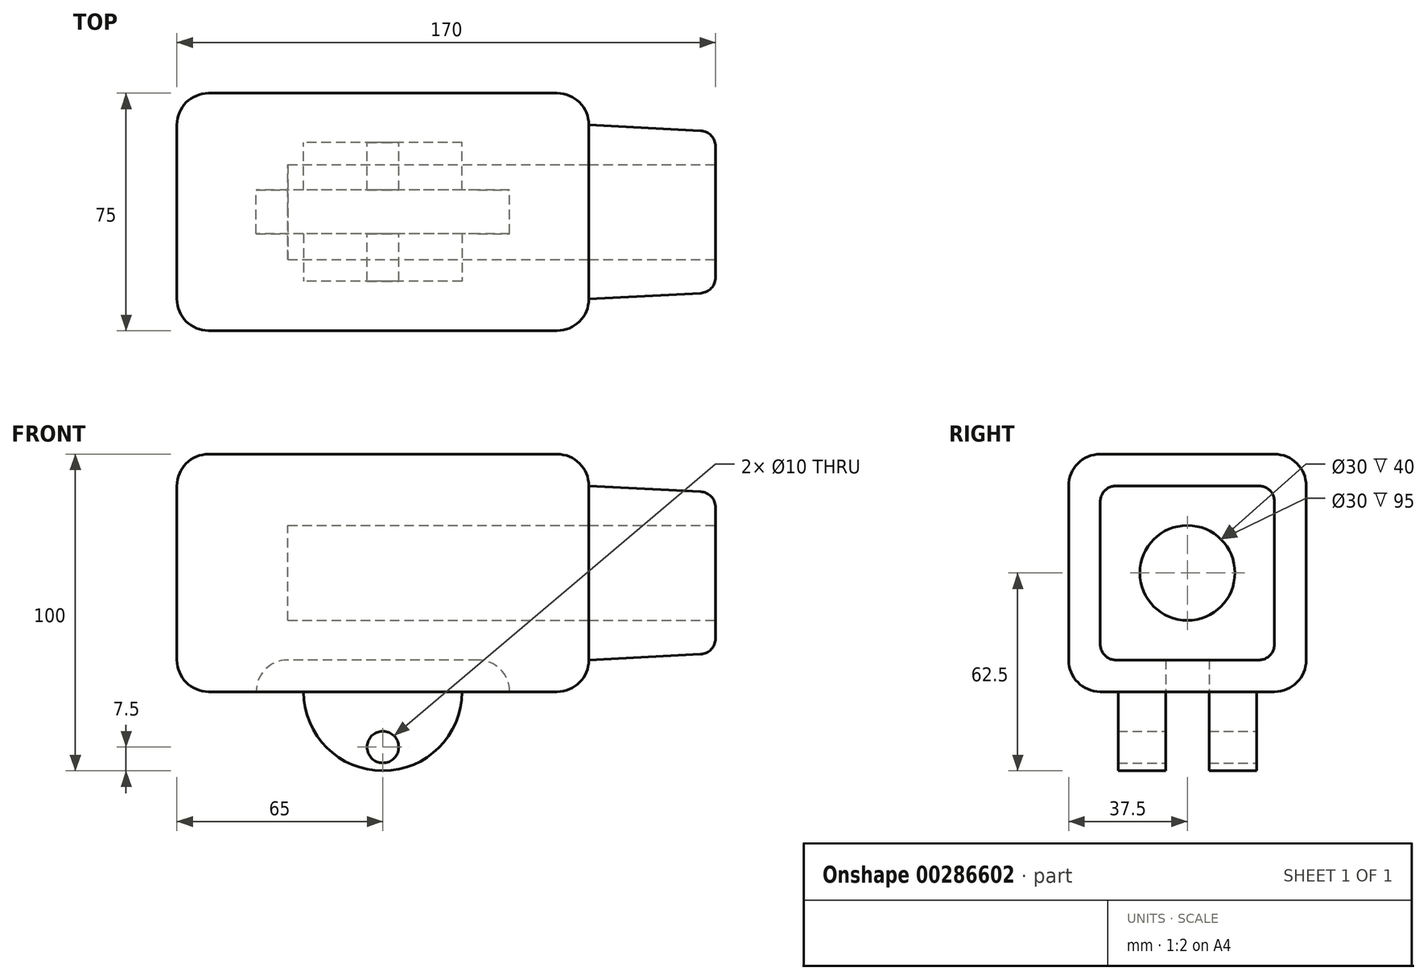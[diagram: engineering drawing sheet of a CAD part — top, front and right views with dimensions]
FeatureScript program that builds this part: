
annotation { "Feature Type Name" : "Feature", "Feature Type Description" : "" }
export const myFeature = defineFeature(function(context is Context, id is Id, definition is map)
    precondition{}
    {
        {
            var Q0;
            Q0=qCreatedBy(makeId("Top.planeOp"),FACE);
            var sketch = newSketch(context, id + "F0", { "sketchPlane" : qUnion([Q0])});
            skLineSegment(sketch, "E0.bottom", {"start": v(-65, 37.5) * mm, "end": v(65, 37.5) * mm});
            skLineSegment(sketch, "E0.top", {"start": v(-65, -37.5) * mm, "end": v(65, -37.5) * mm});
            skLineSegment(sketch, "E0.left", {"start": v(-65, 37.5) * mm, "end": v(-65, -37.5) * mm});
            skLineSegment(sketch, "E0.right", {"start": v(65, 37.5) * mm, "end": v(65, -37.5) * mm});
            skPoint(sketch, "E0.middle", {"position": v(0, 0) * mm});
            skSolve(sketch);
        }
        {
            var Q0;
            Q0=makeQuery(id+"F0.imprint","IMPRINT",FACE,{"disambiguationData":[TD([[makeQuery(id+"F0.imprint","IMPRINT",EDGE,{"derivedFrom":sQuery(id+"F0.wireOp",EDGE,"E0.bottom")}),-1.0]])]});
            extrude(context, id + "F1", {"entities" : qUnion([Q0]), "depth" : 75 * mm});
        }
        {
            var Q0;
            Q0=makeQuery(id+"F1.opExtrude","CAP_FACE",FACE,{"disambiguationData":[OSD([sQuery(id+"F0.wireOp",EDGE,"E0.bottom"),sQuery(id+"F0.wireOp",EDGE,"E0.top"),sQuery(id+"F0.wireOp",EDGE,"E0.left"),sQuery(id+"F0.wireOp",EDGE,"E0.right")])],"isStart":false});
            var Q1;
            Q1=makeQuery(id+"F1.opExtrude","SWEPT_FACE",FACE,{"disambiguationData":[OSD([sQuery(id+"F0.wireOp",EDGE,"E0.top")])]});
            var Q2;
            Q2=makeQuery(id+"F1.opExtrude","SWEPT_FACE",FACE,{"disambiguationData":[OSD([sQuery(id+"F0.wireOp",EDGE,"E0.right")])]});
            var Q3;
            Q3=makeQuery(id+"F1.opExtrude","SWEPT_FACE",FACE,{"disambiguationData":[OSD([sQuery(id+"F0.wireOp",EDGE,"E0.bottom")])]});
            var Q4;
            Q4=makeQuery(id+"F1.opExtrude","CAP_FACE",FACE,{"disambiguationData":[OSD([sQuery(id+"F0.wireOp",EDGE,"E0.bottom"),sQuery(id+"F0.wireOp",EDGE,"E0.top"),sQuery(id+"F0.wireOp",EDGE,"E0.left"),sQuery(id+"F0.wireOp",EDGE,"E0.right")])],"isStart":true});
            fillet(context, id + "F2", {"entities" : qUnion([Q0, Q1, Q2, Q3, Q4]), "radius" : 10 * mm, "tangentPropagation" : true, "allowEdgeOverflow" : false});
        }
        {
            var Q0;
            Q0=makeQuery(id+"F1.opExtrude","SWEPT_FACE",FACE,{"disambiguationData":[OSD([sQuery(id+"F0.wireOp",EDGE,"E0.right")])]});
            extrude(context, id + "F3", {"entities" : qUnion([Q0]), "depth" : 40 * mm, "hasDraft" : true, "draftAngle" : 3 * degree, "draftPullDirection" : true});
        }
        {
            var Q0;
            {var subQ0=sQuery(id+"F0.wireOp",EDGE,"E0.right");var subQ1=sQuery(id+"F0.wireOp",EDGE,"E0.top");Q0=makeQuery(id+"F3.opExtrude","SWEPT_EDGE",EDGE,{"disambiguationData":[OSD([subQ1,subQ0]),TDD([makeQuery(id+"F2.opFillet","BLEND_VERTEX",VERTEX,{"blendedFrom":[makeQuery(id+"F1.opExtrude","CAP_VERTEX",VERTEX,{"disambiguationData":[OSD([subQ1,subQ0])],"isStart":false}),makeQuery(id+"F1.opExtrude","SWEPT_EDGE",EDGE,{"disambiguationData":[OSD([subQ1,subQ0])]}),makeQuery(id+"F1.opExtrude","CAP_EDGE",EDGE,{"disambiguationData":[OSD([subQ0])],"isStart":false}),makeQuery(id+"F1.opExtrude","SWEPT_FACE",FACE,{"disambiguationData":[OSD([subQ0])]})],"blendedInto":[makeQuery(id+"F1.opExtrude","SWEPT_FACE",FACE,{"disambiguationData":[OSD([subQ0])]})]})])]});}
            var Q1;
            {var subQ0=sQuery(id+"F0.wireOp",EDGE,"E0.right");var subQ1=sQuery(id+"F0.wireOp",EDGE,"E0.bottom");Q1=makeQuery(id+"F3.opExtrude","SWEPT_EDGE",EDGE,{"disambiguationData":[OSD([subQ1,subQ0]),TDD([makeQuery(id+"F2.opFillet","BLEND_VERTEX",VERTEX,{"blendedFrom":[makeQuery(id+"F1.opExtrude","CAP_VERTEX",VERTEX,{"disambiguationData":[OSD([subQ1,subQ0])],"isStart":false}),makeQuery(id+"F1.opExtrude","SWEPT_EDGE",EDGE,{"disambiguationData":[OSD([subQ1,subQ0])]}),makeQuery(id+"F1.opExtrude","CAP_EDGE",EDGE,{"disambiguationData":[OSD([subQ0])],"isStart":false}),makeQuery(id+"F1.opExtrude","SWEPT_FACE",FACE,{"disambiguationData":[OSD([subQ0])]})],"blendedInto":[makeQuery(id+"F1.opExtrude","SWEPT_FACE",FACE,{"disambiguationData":[OSD([subQ0])]})]})])]});}
            var Q2;
            {var subQ0=sQuery(id+"F0.wireOp",EDGE,"E0.right");var subQ1=sQuery(id+"F0.wireOp",EDGE,"E0.bottom");Q2=makeQuery(id+"F3.opExtrude","SWEPT_EDGE",EDGE,{"disambiguationData":[OSD([subQ1,subQ0]),TDD([makeQuery(id+"F2.opFillet","BLEND_VERTEX",VERTEX,{"blendedFrom":[makeQuery(id+"F1.opExtrude","CAP_VERTEX",VERTEX,{"disambiguationData":[OSD([subQ1,subQ0])],"isStart":true}),makeQuery(id+"F1.opExtrude","SWEPT_EDGE",EDGE,{"disambiguationData":[OSD([subQ1,subQ0])]}),makeQuery(id+"F1.opExtrude","CAP_EDGE",EDGE,{"disambiguationData":[OSD([subQ0])],"isStart":true}),makeQuery(id+"F1.opExtrude","SWEPT_FACE",FACE,{"disambiguationData":[OSD([subQ0])]})],"blendedInto":[makeQuery(id+"F1.opExtrude","SWEPT_FACE",FACE,{"disambiguationData":[OSD([subQ0])]})]})])]});}
            var Q3;
            {var subQ0=sQuery(id+"F0.wireOp",EDGE,"E0.right");var subQ1=sQuery(id+"F0.wireOp",EDGE,"E0.top");Q3=makeQuery(id+"F3.opExtrude","SWEPT_EDGE",EDGE,{"disambiguationData":[OSD([subQ1,subQ0]),TDD([makeQuery(id+"F2.opFillet","BLEND_VERTEX",VERTEX,{"blendedFrom":[makeQuery(id+"F1.opExtrude","CAP_VERTEX",VERTEX,{"disambiguationData":[OSD([subQ1,subQ0])],"isStart":true}),makeQuery(id+"F1.opExtrude","SWEPT_EDGE",EDGE,{"disambiguationData":[OSD([subQ1,subQ0])]}),makeQuery(id+"F1.opExtrude","CAP_EDGE",EDGE,{"disambiguationData":[OSD([subQ0])],"isStart":true}),makeQuery(id+"F1.opExtrude","SWEPT_FACE",FACE,{"disambiguationData":[OSD([subQ0])]})],"blendedInto":[makeQuery(id+"F1.opExtrude","SWEPT_FACE",FACE,{"disambiguationData":[OSD([subQ0])]})]})])]});}
            var Q4;
            Q4=makeQuery(id+"F3.opExtrude","CAP_FACE",FACE,{"disambiguationData":[OSD([sQuery(id+"F0.wireOp",EDGE,"E0.right")])],"isStart":false});
            fillet(context, id + "F4", {"entities" : qUnion([Q0, Q1, Q2, Q3, Q4]), "radius" : 5 * mm, "tangentPropagation" : true, "allowEdgeOverflow" : false});
        }
        {
            var Q0;
            Q0=makeQuery(id+"F3.opExtrude","CAP_FACE",FACE,{"disambiguationData":[OSD([sQuery(id+"F0.wireOp",EDGE,"E0.right")])],"isStart":false});
            var sketch = newSketch(context, id + "F5", { "sketchPlane" : qUnion([Q0])});
            skCircle(sketch, "E1", {"center": v(0, 37.5) * mm, "radius": 15 * mm});
            skPoint(sketch, "E1.centerSnap0", {"position": v(-20.66, 37.5) * mm});
            skSolve(sketch);
        }
        {
            var Q0;
            Q0=makeQuery(id+"F5.imprint","IMPRINT",FACE,{"disambiguationData":[TD([[makeQuery(id+"F5.imprint","IMPRINT",EDGE,{"derivedFrom":sQuery(id+"F5.wireOp",EDGE,"E1")}),1.0]])]});
            extrude(context, id + "F6", {"entities" : qUnion([Q0]), "operationType" : NewBodyOperationType.REMOVE, "oppositeDirection" : true, "depth" : 135 * mm});
        }
        {
            var Q0;
            Q0=makeQuery(id+"F1.opExtrude","CAP_FACE",FACE,{"disambiguationData":[OSD([sQuery(id+"F0.wireOp",EDGE,"E0.bottom"),sQuery(id+"F0.wireOp",EDGE,"E0.top"),sQuery(id+"F0.wireOp",EDGE,"E0.left"),sQuery(id+"F0.wireOp",EDGE,"E0.right")])],"isStart":true});
            var sketch = newSketch(context, id + "F7", { "sketchPlane" : qUnion([Q0])});
            skLineSegment(sketch, "E2.bottom", {"start": v(25, 6.88) * mm, "end": v(-25, 6.88) * mm});
            skLineSegment(sketch, "E2.top", {"start": v(25, 21.88) * mm, "end": v(-25, 21.88) * mm});
            skLineSegment(sketch, "E2.left", {"start": v(25, 6.88) * mm, "end": v(25, 21.88) * mm});
            skLineSegment(sketch, "E2.right", {"start": v(-25, 6.88) * mm, "end": v(-25, 21.88) * mm});
            skPoint(sketch, "E2.middle", {"position": v(0, 14.38) * mm});
            skLineSegment(sketch, "E3.bottom", {"start": v(25, -6.88) * mm, "end": v(-25, -6.88) * mm});
            skLineSegment(sketch, "E3.top", {"start": v(25, -21.88) * mm, "end": v(-25, -21.88) * mm});
            skLineSegment(sketch, "E3.left", {"start": v(25, -6.88) * mm, "end": v(25, -21.88) * mm});
            skLineSegment(sketch, "E3.right", {"start": v(-25, -6.88) * mm, "end": v(-25, -21.88) * mm});
            skPoint(sketch, "E3.middle", {"position": v(0, -14.38) * mm});
            skSolve(sketch);
        }
        {
            var Q0;
            Q0=makeQuery(id+"F7.imprint","IMPRINT",FACE,{"disambiguationData":[TD([[makeQuery(id+"F7.imprint","IMPRINT",EDGE,{"derivedFrom":sQuery(id+"F7.wireOp",EDGE,"E3.bottom")}),1.0]])]});
            var Q1;
            Q1=makeQuery(id+"F7.imprint","IMPRINT",FACE,{"disambiguationData":[TD([[makeQuery(id+"F7.imprint","IMPRINT",EDGE,{"derivedFrom":sQuery(id+"F7.wireOp",EDGE,"E2.bottom")}),-1.0]])]});
            extrude(context, id + "F8", {"entities" : qUnion([Q0, Q1]), "operationType" : NewBodyOperationType.ADD, "depth" : 25 * mm});
        }
        {
            var Q0;
            Q0=makeQuery(id+"F8.opExtrude","CAP_EDGE",EDGE,{"disambiguationData":[OSD([sQuery(id+"F7.wireOp",EDGE,"E3.right")])],"isStart":false});
            var Q1;
            Q1=makeQuery(id+"F8.opExtrude","CAP_EDGE",EDGE,{"disambiguationData":[OSD([sQuery(id+"F7.wireOp",EDGE,"E3.left")])],"isStart":false});
            var Q2;
            Q2=makeQuery(id+"F8.opExtrude","CAP_EDGE",EDGE,{"disambiguationData":[OSD([sQuery(id+"F7.wireOp",EDGE,"E2.left")])],"isStart":false});
            var Q3;
            Q3=makeQuery(id+"F8.opExtrude","CAP_EDGE",EDGE,{"disambiguationData":[OSD([sQuery(id+"F7.wireOp",EDGE,"E2.right")])],"isStart":false});
            fillet(context, id + "F9", {"entities" : qUnion([Q0, Q1, Q2, Q3]), "radius" : 25 * mm, "tangentPropagation" : true, "allowEdgeOverflow" : false});
        }
        {
            var Q0;
            Q0=makeQuery(id+"F8.opExtrude","SWEPT_FACE",FACE,{"disambiguationData":[OSD([sQuery(id+"F7.wireOp",EDGE,"E3.top")])]});
            var sketch = newSketch(context, id + "F10", { "sketchPlane" : qUnion([Q0])});
            skCircle(sketch, "E4", {"center": v(0, -17.5) * mm, "radius": 5 * mm});
            skPoint(sketch, "E4.centerSnap0", {"position": v(0, -25) * mm});
            skSolve(sketch);
        }
        {
            var Q0;
            Q0=makeQuery(id+"F10.imprint","IMPRINT",FACE,{"disambiguationData":[TD([[makeQuery(id+"F10.imprint","IMPRINT",EDGE,{"derivedFrom":sQuery(id+"F10.wireOp",EDGE,"E4")}),1.0]])]});
            extrude(context, id + "F11", {"entities" : qUnion([Q0]), "operationType" : NewBodyOperationType.REMOVE, "endBound" : BoundingType.THROUGH_ALL, "oppositeDirection" : true, "depth" : 25 * mm});
        }
        {
            var Q0;
            Q0=makeQuery(id+"F1.opExtrude","CAP_FACE",FACE,{"disambiguationData":[OSD([sQuery(id+"F0.wireOp",EDGE,"E0.bottom"),sQuery(id+"F0.wireOp",EDGE,"E0.top"),sQuery(id+"F0.wireOp",EDGE,"E0.left"),sQuery(id+"F0.wireOp",EDGE,"E0.right")])],"isStart":true});
            var sketch = newSketch(context, id + "F12", { "sketchPlane" : qUnion([Q0])});
            skLineSegment(sketch, "E5.bottom", {"start": v(40, 6.88) * mm, "end": v(-40, 6.88) * mm});
            skLineSegment(sketch, "E5.top", {"start": v(40, -6.88) * mm, "end": v(-40, -6.88) * mm});
            skLineSegment(sketch, "E5.left", {"start": v(40, 6.88) * mm, "end": v(40, -6.88) * mm});
            skLineSegment(sketch, "E5.right", {"start": v(-40, 6.88) * mm, "end": v(-40, -6.88) * mm});
            skPoint(sketch, "E5.middle", {"position": v(0, 0) * mm});
            skSolve(sketch);
        }
        {
            var Q0;
            {var subQ3=sQuery(id+"F12.wireOp",EDGE,"E5.left");Q0=makeQuery(id+"F12.imprint","IMPRINT",FACE,{"disambiguationData":[TD([[makeQuery(id+"F12.imprint","IMPRINT",EDGE,{"derivedFrom":subQ3}),-1.0]])]});}
            extrude(context, id + "F13", {"entities" : qUnion([Q0]), "operationType" : NewBodyOperationType.REMOVE, "oppositeDirection" : true, "depth" : 10 * mm});
        }
        {
            var Q0;
            Q0=makeQuery(id+"F13.boolean.opBoolean","COPY",EDGE,{"derivedFrom":makeQuery(id+"F13.opExtrude","CAP_EDGE",EDGE,{"disambiguationData":[OSD([sQuery(id+"F12.wireOp",EDGE,"E5.right")])],"isStart":false})});
            var Q1;
            Q1=makeQuery(id+"F13.boolean.opBoolean","COPY",EDGE,{"derivedFrom":makeQuery(id+"F13.opExtrude","CAP_EDGE",EDGE,{"disambiguationData":[OSD([sQuery(id+"F12.wireOp",EDGE,"E5.left")])],"isStart":false})});
            fillet(context, id + "F14", {"entities" : qUnion([Q0, Q1]), "radius" : 10 * mm, "tangentPropagation" : true, "allowEdgeOverflow" : false});
        }
    });
